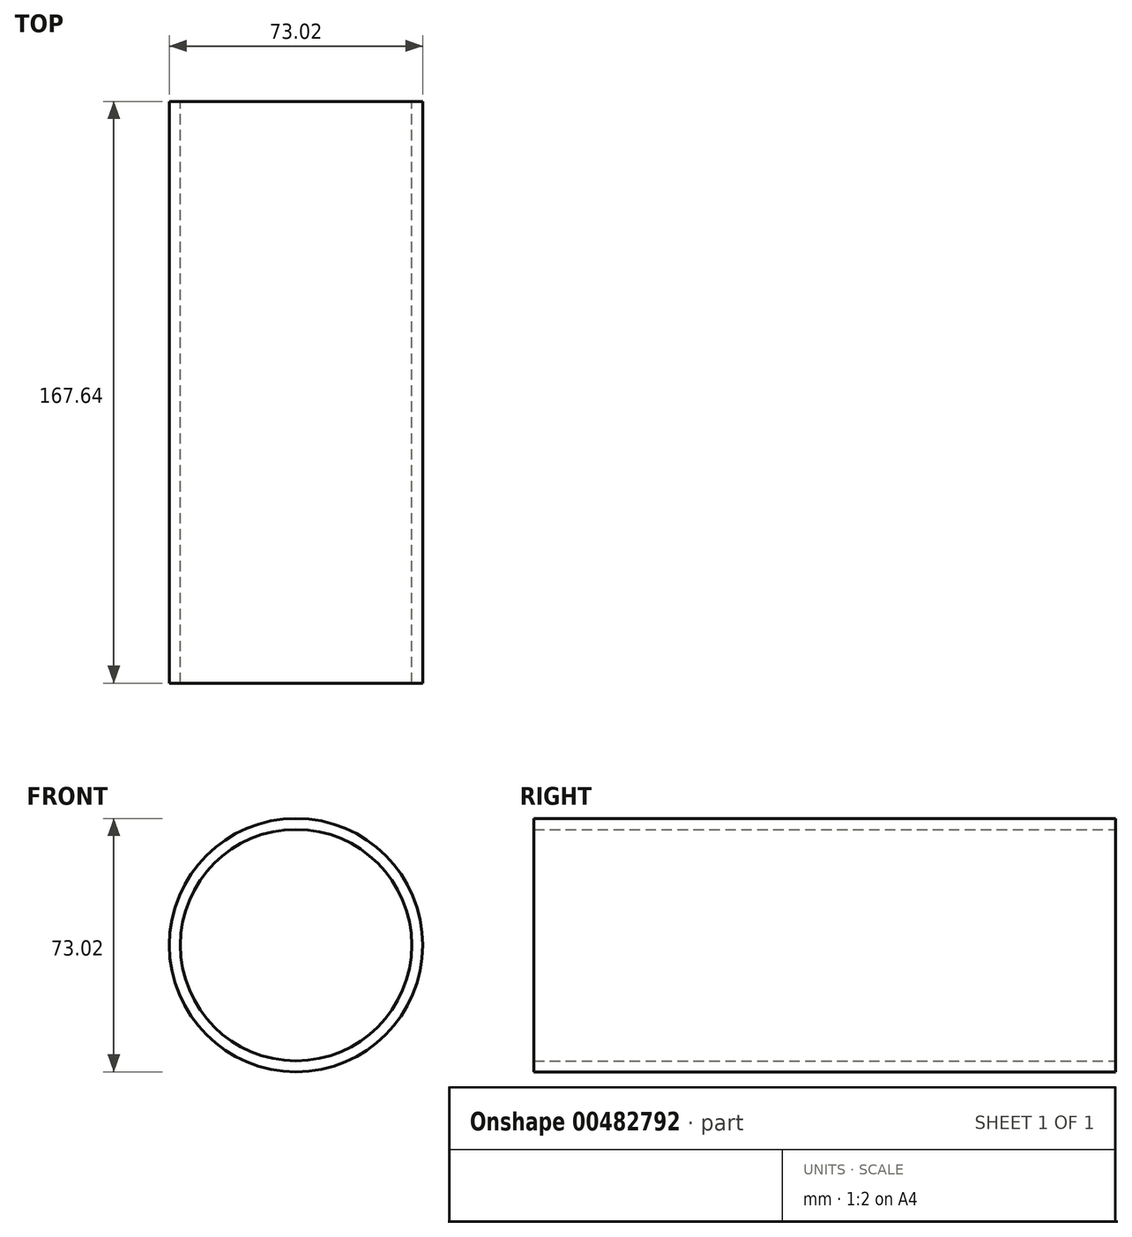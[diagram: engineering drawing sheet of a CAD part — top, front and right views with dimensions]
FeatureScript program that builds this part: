
annotation { "Feature Type Name" : "Feature", "Feature Type Description" : "" }
export const myFeature = defineFeature(function(context is Context, id is Id, definition is map)
    precondition{}
    {
        {
            var Q0;
            Q0=qCreatedBy(makeId("Front.planeOp"),FACE);
            var sketch = newSketch(context, id + "F0", { "sketchPlane" : qUnion([Q0])});
            skCircle(sketch, "E0", {"center": v(0, 0) * mm, "radius": 36.51 * mm});
            skCircle(sketch, "E1", {"center": v(0, 0) * mm, "radius": 33.34 * mm});
            skSolve(sketch);
        }
        {
            var Q0;
            Q0=makeQuery(id+"F0.imprint","IMPRINT",FACE,{"disambiguationData":[TD([[makeQuery(id+"F0.imprint","IMPRINT",EDGE,{"derivedFrom":sQuery(id+"F0.wireOp",EDGE,"E0")}),1.0]])]});
            extrude(context, id + "F1", {"entities" : qUnion([Q0]), "depth" : 167.64 * mm});
        }
    });
